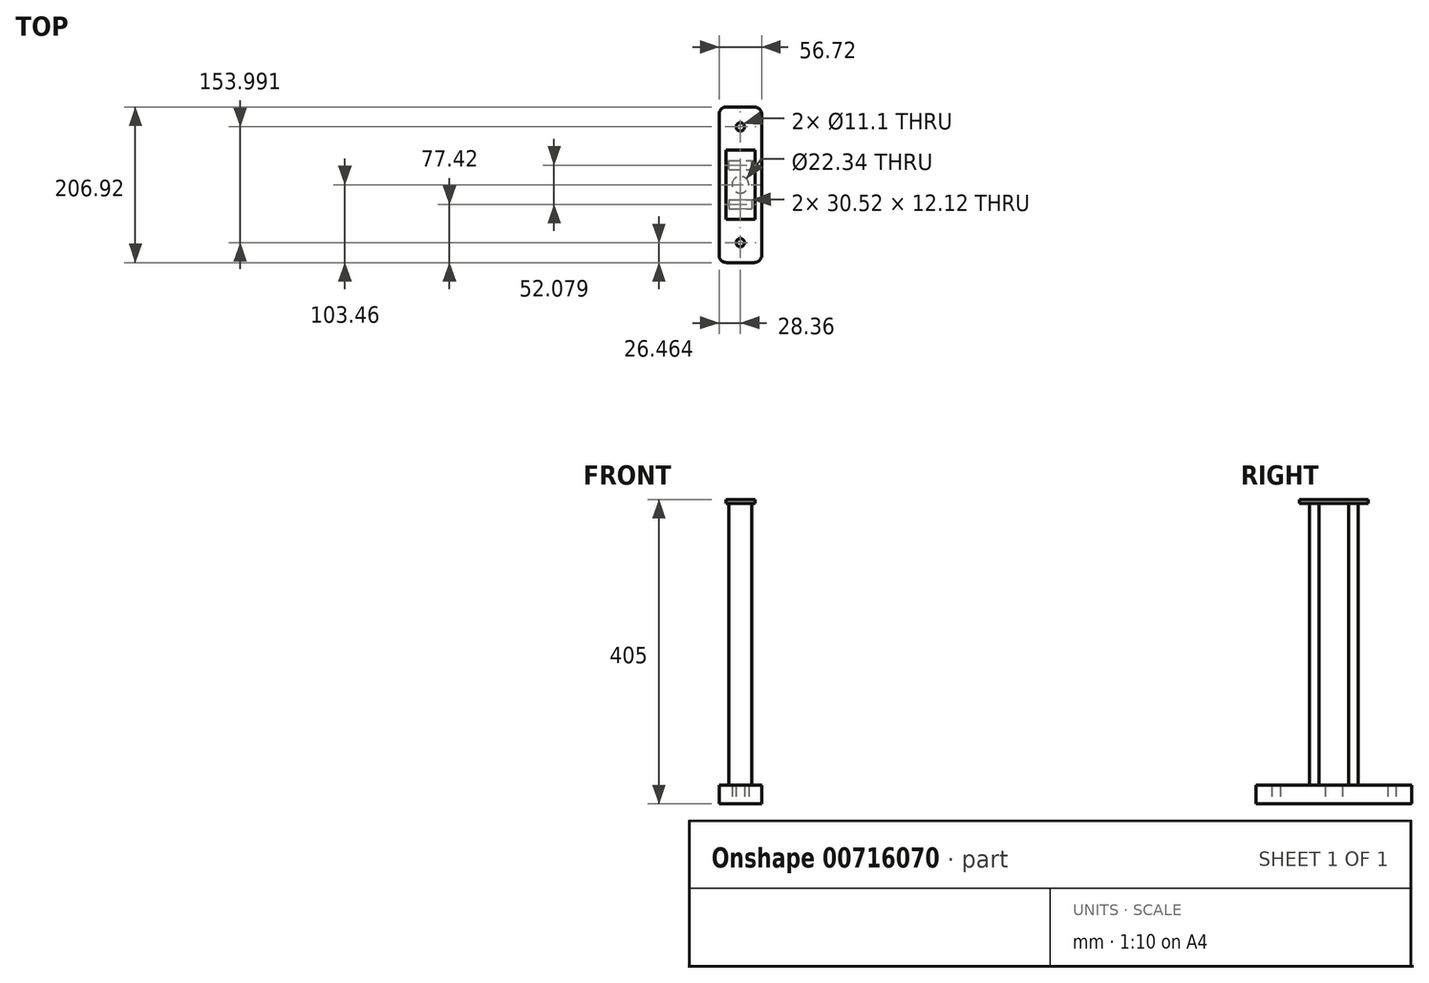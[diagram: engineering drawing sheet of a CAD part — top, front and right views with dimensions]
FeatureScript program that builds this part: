
annotation { "Feature Type Name" : "Feature", "Feature Type Description" : "" }
export const myFeature = defineFeature(function(context is Context, id is Id, definition is map)
    precondition{}
    {
        {
            var Q0;
            Q0=qCreatedBy(makeId("Top.planeOp"),FACE);
            var sketch = newSketch(context, id + "F0", { "sketchPlane" : qUnion([Q0])});
            skLineSegment(sketch, "E0.bottom", {"start": v(18.36, 103.46) * mm, "end": v(-18.36, 103.46) * mm});
            skLineSegment(sketch, "E0.top", {"start": v(18.36, -103.46) * mm, "end": v(-18.36, -103.46) * mm});
            skLineSegment(sketch, "E0.left", {"start": v(28.36, 93.46) * mm, "end": v(28.36, -93.46) * mm});
            skLineSegment(sketch, "E0.right", {"start": v(-28.36, 93.46) * mm, "end": v(-28.36, -93.46) * mm});
            skPoint(sketch, "E0.middle", {"position": v(0, 0) * mm});
            skPoint(sketch, "E1.visualSharp", {"position": v(-28.36, 103.46) * mm});
            skArc(sketch, "E1.filletArc", {"start": v(-18.36, 103.46) * mm, "mid": v(-25.43, 100.53) * mm, "end": v(-28.36, 93.46) * mm});
            skPoint(sketch, "E2.visualSharp", {"position": v(28.36, 103.46) * mm});
            skArc(sketch, "E2.filletArc", {"start": v(28.36, 93.46) * mm, "mid": v(25.43, 100.53) * mm, "end": v(18.36, 103.46) * mm});
            skPoint(sketch, "E3.visualSharp", {"position": v(28.36, -103.46) * mm});
            skArc(sketch, "E3.filletArc", {"start": v(18.36, -103.46) * mm, "mid": v(25.43, -100.53) * mm, "end": v(28.36, -93.46) * mm});
            skPoint(sketch, "E4.visualSharp", {"position": v(-28.36, -103.46) * mm});
            skArc(sketch, "E4.filletArc", {"start": v(-28.36, -93.46) * mm, "mid": v(-25.43, -100.53) * mm, "end": v(-18.36, -103.46) * mm});
            skCircle(sketch, "E5", {"center": v(0, 0) * mm, "radius": 11.17 * mm});
            skCircle(sketch, "E6", {"center": v(0, 77) * mm, "radius": 5.55 * mm});
            skCircle(sketch, "E7.MirrorC", {"center": v(0, -77) * mm, "radius": 5.55 * mm});
            skLineSegment(sketch, "E8.bottom", {"start": v(15.26, 32.1) * mm, "end": v(-15.26, 32.1) * mm});
            skLineSegment(sketch, "E8.top", {"start": v(15.26, 19.98) * mm, "end": v(-15.26, 19.98) * mm});
            skLineSegment(sketch, "E8.left", {"start": v(15.26, 32.1) * mm, "end": v(15.26, 19.98) * mm});
            skLineSegment(sketch, "E8.right", {"start": v(-15.26, 32.1) * mm, "end": v(-15.26, 19.98) * mm});
            skPoint(sketch, "E8.middle", {"position": v(0, 26.04) * mm});
            skLineSegment(sketch, "E9.MirrorCS", {"start": v(15.26, -19.98) * mm, "end": v(-15.26, -19.98) * mm});
            skPoint(sketch, "E10.MirrorP", {"position": v(0, -26.04) * mm});
            skLineSegment(sketch, "E11.MirrorCS", {"start": v(15.26, -32.1) * mm, "end": v(15.26, -19.98) * mm});
            skLineSegment(sketch, "E12.MirrorCS", {"start": v(15.26, -32.1) * mm, "end": v(-15.26, -32.1) * mm});
            skLineSegment(sketch, "E13.MirrorCS", {"start": v(-15.26, -32.1) * mm, "end": v(-15.26, -19.98) * mm});
            skSolve(sketch);
        }
        {
            var Q0;
            Q0=makeQuery(id+"F0.imprint","IMPRINT",FACE,{"disambiguationData":[TD([[makeQuery(id+"F0.imprint","IMPRINT",EDGE,{"derivedFrom":sQuery(id+"F0.wireOp",EDGE,"E0.bottom")}),1.0]])]});
            var Q1;
            Q1=makeQuery(id+"F0.imprint","IMPRINT",FACE,{"disambiguationData":[TD([[makeQuery(id+"F0.imprint","IMPRINT",EDGE,{"derivedFrom":sQuery(id+"F0.wireOp",EDGE,"E9.MirrorCS")}),1.0]])]});
            var Q2;
            Q2=makeQuery(id+"F0.imprint","IMPRINT",FACE,{"disambiguationData":[TD([[makeQuery(id+"F0.imprint","IMPRINT",EDGE,{"derivedFrom":sQuery(id+"F0.wireOp",EDGE,"E8.bottom")}),1.0]])]});
            extrude(context, id + "F1", {"entities" : qUnion([Q0, Q1, Q2]), "depth" : 25 * mm, "offsetDistance" : 25 * mm});
        }
        {
            var Q0;
            Q0=makeQuery(id+"F0.imprint","IMPRINT",FACE,{"disambiguationData":[TD([[makeQuery(id+"F0.imprint","IMPRINT",EDGE,{"derivedFrom":sQuery(id+"F0.wireOp",EDGE,"E9.MirrorCS")}),1.0]])]});
            var Q1;
            Q1=makeQuery(id+"F0.imprint","IMPRINT",FACE,{"disambiguationData":[TD([[makeQuery(id+"F0.imprint","IMPRINT",EDGE,{"derivedFrom":sQuery(id+"F0.wireOp",EDGE,"E8.bottom")}),1.0]])]});
            extrude(context, id + "F2", {"entities" : qUnion([Q0, Q1]), "operationType" : NewBodyOperationType.ADD, "depth" : 400 * mm, "offsetDistance" : 25 * mm});
        }
        {
            var Q0;
            Q0=makeQuery(id+"F2.opExtrude","CAP_FACE",FACE,{"disambiguationData":[OSD([sQuery(id+"F0.wireOp",EDGE,"E8.bottom"),sQuery(id+"F0.wireOp",EDGE,"E8.top"),sQuery(id+"F0.wireOp",EDGE,"E8.left"),sQuery(id+"F0.wireOp",EDGE,"E8.right")])],"isStart":false});
            var sketch = newSketch(context, id + "F3", { "sketchPlane" : qUnion([Q0])});
            skLineSegment(sketch, "E14.bottom", {"start": v(19.3, 45.84) * mm, "end": v(-19.3, 45.84) * mm});
            skLineSegment(sketch, "E14.top", {"start": v(19.3, -45.84) * mm, "end": v(-19.3, -45.84) * mm});
            skLineSegment(sketch, "E14.left", {"start": v(19.3, 45.84) * mm, "end": v(19.3, -45.84) * mm});
            skLineSegment(sketch, "E14.right", {"start": v(-19.3, 45.84) * mm, "end": v(-19.3, -45.84) * mm});
            skPoint(sketch, "E14.middle", {"position": v(0, 0) * mm});
            skSolve(sketch);
        }
        {
            var Q0;
            Q0 = qSketchRegion(id + "F3", true);
            extrude(context, id + "F4", {"entities" : qUnion([Q0]), "operationType" : NewBodyOperationType.ADD, "depth" : 5 * mm, "offsetDistance" : 25 * mm});
        }
    });
